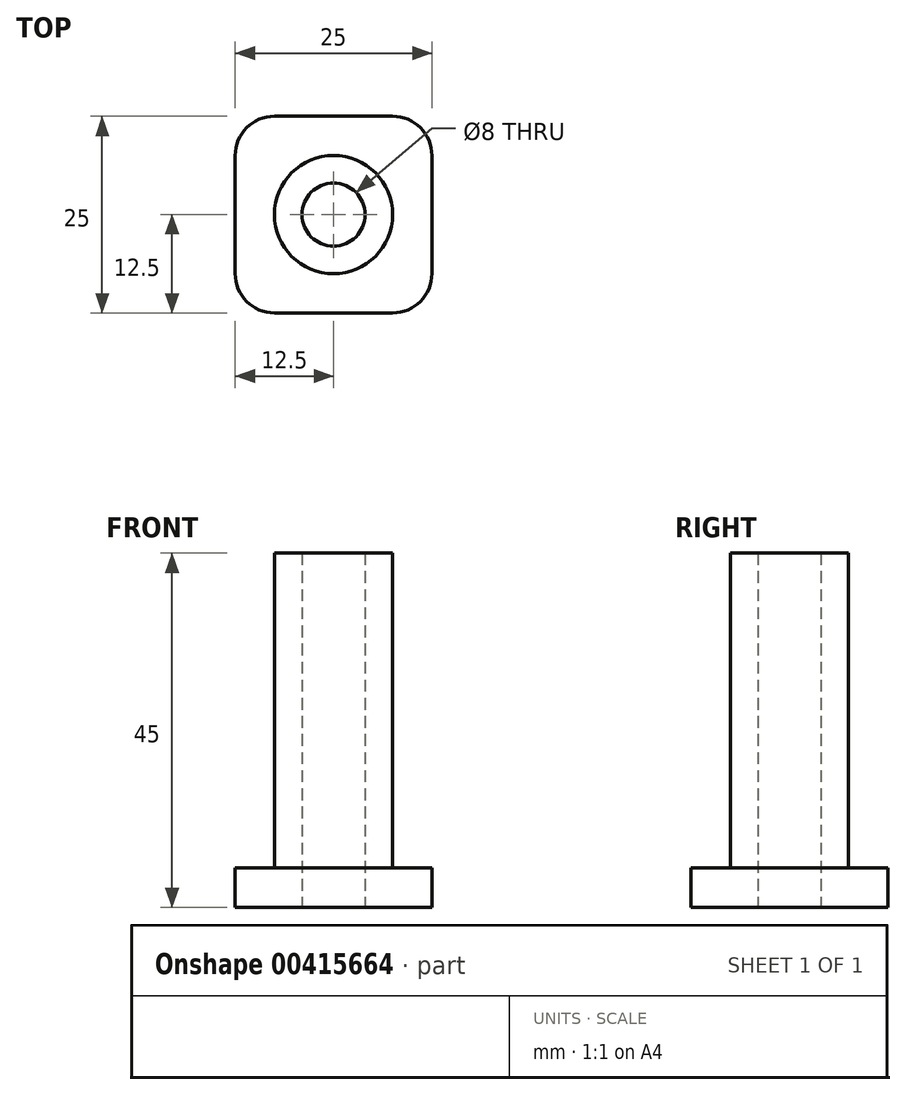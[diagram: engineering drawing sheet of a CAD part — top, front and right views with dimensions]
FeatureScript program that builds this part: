
annotation { "Feature Type Name" : "Feature", "Feature Type Description" : "" }
export const myFeature = defineFeature(function(context is Context, id is Id, definition is map)
    precondition{}
    {
        {
            var Q0;
            Q0=qCreatedBy(makeId("Top.planeOp"),FACE);
            var sketch = newSketch(context, id + "F0", { "sketchPlane" : qUnion([Q0])});
            skCircle(sketch, "E0", {"center": v(0, 0) * mm, "radius": 7.5 * mm});
            skCircle(sketch, "E1", {"center": v(0, 0) * mm, "radius": 4 * mm});
            skSolve(sketch);
        }
        {
            var Q0;
            Q0=qCreatedBy(makeId("Top.planeOp"),FACE);
            var sketch = newSketch(context, id + "F1", { "sketchPlane" : qUnion([Q0])});
            skLineSegment(sketch, "E2", {"start": v(0, 0) * mm, "end": v(0, -12.5) * mm});
            skLineSegment(sketch, "E3", {"start": v(0, -12.5) * mm, "end": v(-12.5, -12.5) * mm});
            skLineSegment(sketch, "E4.bottom", {"start": v(-12.5, -12.5) * mm, "end": v(12.5, -12.5) * mm});
            skLineSegment(sketch, "E4.top", {"start": v(-12.5, 12.5) * mm, "end": v(12.5, 12.5) * mm});
            skLineSegment(sketch, "E4.left", {"start": v(-12.5, -12.5) * mm, "end": v(-12.5, 12.5) * mm});
            skLineSegment(sketch, "E4.right", {"start": v(12.5, -12.5) * mm, "end": v(12.5, 12.5) * mm});
            skSolve(sketch);
        }
        {
            var Q0;
            Q0=makeQuery(id+"F1.imprint","IMPRINT",FACE,{"disambiguationData":[TD([[makeQuery(id+"F1.imprint","IMPRINT",EDGE,{"derivedFrom":sQuery(id+"F1.wireOp",EDGE,"E4.top")}),-1.0]])]});
            extrude(context, id + "F2", {"entities" : qUnion([Q0]), "depth" : 5 * mm});
        }
        {
            var Q0;
            Q0 = qSketchRegion(id + "F0", true);
            var Q1;
            Q1=sQuery(id+"F0.wireOp",EDGE,"E0");
            extrude(context, id + "F3", {"entities" : qUnion([Q0]), "operationType" : NewBodyOperationType.ADD, "surfaceEntities" : qUnion([Q1]), "depth" : 45 * mm});
        }
        {
            var Q0;
            Q0=makeQuery(id+"F2.opExtrude","SWEPT_EDGE",EDGE,{"disambiguationData":[OSD([sQuery(id+"F1.wireOp",EDGE,"E4.top"),sQuery(id+"F1.wireOp",EDGE,"E4.right")])]});
            var Q1;
            Q1=makeQuery(id+"F2.opExtrude","SWEPT_EDGE",EDGE,{"disambiguationData":[OSD([sQuery(id+"F1.wireOp",EDGE,"E4.top"),sQuery(id+"F1.wireOp",EDGE,"E4.left")])]});
            var Q2;
            Q2=makeQuery(id+"F2.opExtrude","SWEPT_EDGE",EDGE,{"disambiguationData":[OSD([sQuery(id+"F1.wireOp",EDGE,"E4.bottom"),sQuery(id+"F1.wireOp",EDGE,"E4.right")])]});
            var Q3;
            Q3=makeQuery(id+"F2.opExtrude","SWEPT_EDGE",EDGE,{"disambiguationData":[OSD([sQuery(id+"F1.wireOp",EDGE,"E4.bottom"),sQuery(id+"F1.wireOp",EDGE,"E4.left")])]});
            fillet(context, id + "F4", {"entities" : qUnion([Q0, Q1, Q2, Q3]), "radius" : 5 * mm, "tangentPropagation" : true, "allowEdgeOverflow" : false});
        }
        {
            var Q0;
            Q0=makeQuery(id+"F0.imprint","IMPRINT",FACE,{"disambiguationData":[TD([[makeQuery(id+"F0.imprint","IMPRINT",EDGE,{"derivedFrom":sQuery(id+"F0.wireOp",EDGE,"E1")}),1.0]])]});
            var Q1;
            Q1=sQuery(id+"F0.wireOp",EDGE,"E1");
            extrude(context, id + "F5", {"entities" : qUnion([Q0]), "operationType" : NewBodyOperationType.REMOVE, "surfaceEntities" : qUnion([Q1]), "depth" : 45 * mm});
        }
    });
